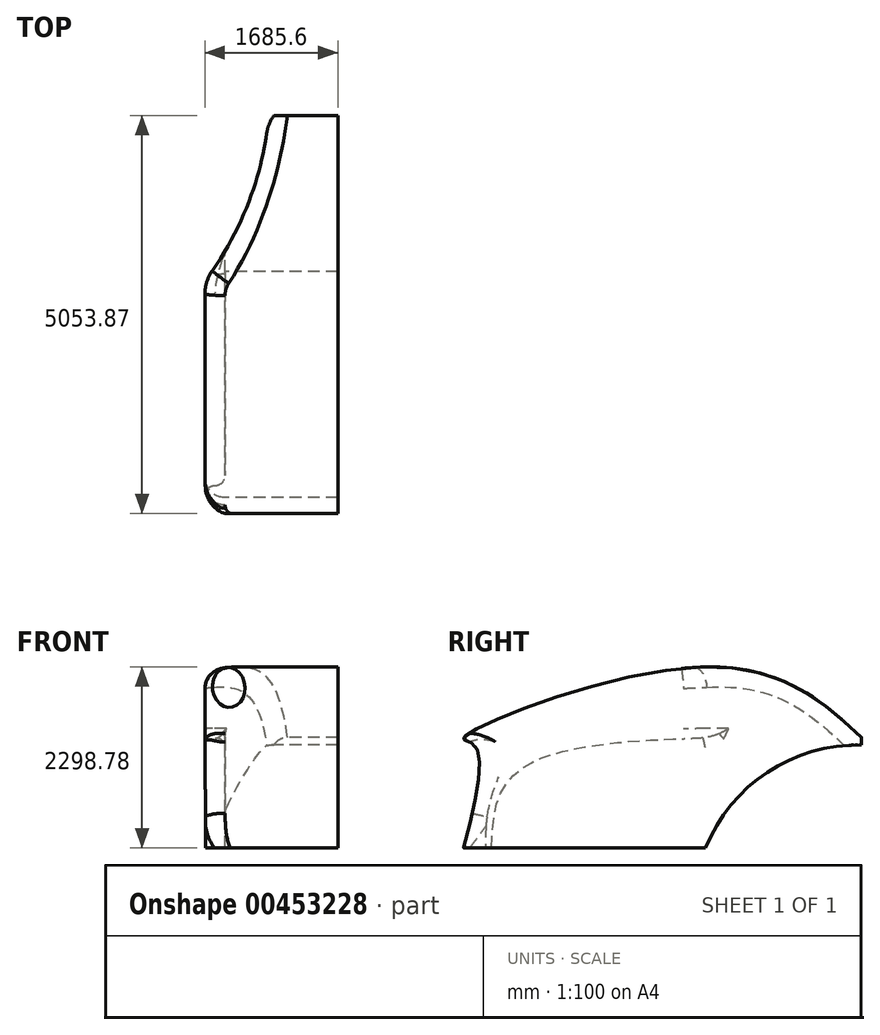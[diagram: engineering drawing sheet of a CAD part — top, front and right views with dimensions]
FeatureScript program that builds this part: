
annotation { "Feature Type Name" : "Feature", "Feature Type Description" : "" }
export const myFeature = defineFeature(function(context is Context, id is Id, definition is map)
    precondition{}
    {
        {
            var Q0;
            Q0=qCreatedBy(makeId("Top.planeOp"),FACE);
            var sketch = newSketch(context, id + "F0", { "sketchPlane" : qUnion([Q0])});
            skLineSegment(sketch, "E0.bottom", {"start": v(-854.4, 72.9) * mm, "end": v(-2159, 72.9) * mm});
            skLineSegment(sketch, "E0.top", {"start": v(-854.4, 5152.9) * mm, "end": v(-1731.8, 5152.9) * mm});
            skLineSegment(sketch, "E0.right", {"start": v(-2540, 453.9) * mm, "end": v(-2540, 2892.85) * mm});
            skPoint(sketch, "E1.visualSharp", {"position": v(-2540, 72.9) * mm});
            skArc(sketch, "E1.filletArc", {"start": v(-2540, 453.9) * mm, "mid": v(-2428.4, 184.5) * mm, "end": v(-2159, 72.9) * mm});
            skArc(sketch, "E2", {"start": v(-2447.98, 3184.45) * mm, "mid": v(-1959.99, 4121.41) * mm, "end": v(-1731.8, 5152.9) * mm});
            skLineSegment(sketch, "E3", {"start": v(-854.4, 5152.9) * mm, "end": v(-854.4, 72.9) * mm});
            skPoint(sketch, "E0.left.end.orphan", {"position": v(23, 5152.9) * mm});
            skPoint(sketch, "E4.visualSharp", {"position": v(-2540, 3058.43) * mm});
            skArc(sketch, "E4.filletArc", {"start": v(-2447.98, 3184.45) * mm, "mid": v(-2516.45, 3045.74) * mm, "end": v(-2540, 2892.85) * mm});
            skSolve(sketch);
        }
        {
            var Q0;
            Q0=makeQuery(id+"F0.imprint","IMPRINT",FACE,{"disambiguationData":[TD([[makeQuery(id+"F0.imprint","IMPRINT",EDGE,{"derivedFrom":sQuery(id+"F0.wireOp",EDGE,"E0.bottom")}),-1.0]])]});
            extrude(context, id + "F1", {"entities" : qUnion([Q0]), "depth" : 2540 * mm});
        }
        {
            var Q0;
            Q0=makeQuery(id+"F1.opExtrude","SWEPT_FACE",FACE,{"disambiguationData":[OSD([sQuery(id+"F0.wireOp",EDGE,"E0.right")])]});
            var sketch = newSketch(context, id + "F2", { "sketchPlane" : qUnion([Q0])});
            skArc(sketch, "E5", {"start": v(-3170.36, 0) * mm, "mid": v(-4005.04, 991.77) * mm, "end": v(-5263.88, 1301.03) * mm});
            skPoint(sketch, "E6.3.internal.snap0", {"position": v(-4005.04, 991.77) * mm});
            skPoint(sketch, "E6.3.internal.orphan", {"position": v(-99.2, 991.77) * mm});
            skFitSpline(sketch, "E7", {"points": [v(-5263.88, 1301.03) * mm, v(-3180.23, 2298.41) * mm, v(-99.2, 1389.9) * mm, v(-237.45, 1301.03) * mm, v(-99.2, 0) * mm], "startDerivative": vector(5128.45, 4861.95) * mm, "endDerivative": vector(1834.22, -7313.57) * mm});
            skLineSegment(sketch, "E8.bottom", {"start": v(-5431.75, -160.49) * mm, "end": v(750.06, -160.49) * mm});
            skLineSegment(sketch, "E8.top", {"start": v(-5431.75, 3009.42) * mm, "end": v(750.06, 3009.42) * mm});
            skLineSegment(sketch, "E8.left", {"start": v(-5431.75, -160.49) * mm, "end": v(-5431.75, 3009.42) * mm});
            skLineSegment(sketch, "E8.right", {"start": v(750.06, -160.49) * mm, "end": v(750.06, 3009.42) * mm});
            skLineSegment(sketch, "E9", {"start": v(-3170.36, 0) * mm, "end": v(-99.2, 0) * mm});
            skSolve(sketch);
        }
        {
            var Q0;
            {var subQ1=sQuery(id+"F0.wireOp",EDGE,"E0.right");var subQ6=makeQuery(id+"F1.opExtrude","CAP_EDGE",EDGE,{"disambiguationData":[OSD([subQ1])],"isStart":false});Q0=makeQuery(id+"F2.imprint","IMPRINT",FACE,{"disambiguationData":[TD([[makeQuery(id+"F2.imprint","IMPRINT",EDGE,{"derivedFrom":subQ6}),1.0]])]});}
            var Q1;
            {var subQ8=sQuery(id+"F2.wireOp",EDGE,"E5");Q1=makeQuery(id+"F2.imprint","IMPRINT",FACE,{"disambiguationData":[TD([[makeQuery(id+"F2.imprint","IMPRINT",EDGE,{"derivedFrom":subQ8}),1.0]])]});}
            extrude(context, id + "F3", {"entities" : qUnion([Q0, Q1]), "operationType" : NewBodyOperationType.REMOVE, "endBound" : BoundingType.THROUGH_ALL, "oppositeDirection" : true, "depth" : 25.4 * mm});
        }
        {
            var Q0;
            Q0=makeQuery(id+"F3.boolean.opBoolean","INTERSECT",EDGE,{"derivedFrom":[makeQuery(id+"F1.opExtrude","SWEPT_FACE",FACE,{"disambiguationData":[OSD([sQuery(id+"F0.wireOp",EDGE,"E2")])]}),makeQuery(id+"F3.opExtrude","SWEPT_FACE",FACE,{"disambiguationData":[OSD([sQuery(id+"F2.wireOp",EDGE,"E7")])]})]});
            var Q1;
            Q1=makeQuery(id+"F3.boolean.opBoolean","INTERSECT",EDGE,{"derivedFrom":[makeQuery(id+"F1.opExtrude","SWEPT_FACE",FACE,{"disambiguationData":[OSD([sQuery(id+"F0.wireOp",EDGE,"E4.filletArc")])]}),makeQuery(id+"F3.opExtrude","SWEPT_FACE",FACE,{"disambiguationData":[OSD([sQuery(id+"F2.wireOp",EDGE,"E7")])]})]});
            var Q2;
            Q2=makeQuery(id+"F3.boolean.opBoolean","COPY",EDGE,{"derivedFrom":makeQuery(id+"F3.opExtrude","CAP_EDGE",EDGE,{"disambiguationData":[OSD([sQuery(id+"F2.wireOp",EDGE,"E7")])],"isStart":true})});
            var Q3;
            Q3=makeQuery(id+"F3.boolean.opBoolean","INTERSECT",EDGE,{"derivedFrom":[makeQuery(id+"F1.opExtrude","SWEPT_FACE",FACE,{"disambiguationData":[OSD([sQuery(id+"F0.wireOp",EDGE,"E1.filletArc")])]}),makeQuery(id+"F3.opExtrude","SWEPT_FACE",FACE,{"disambiguationData":[OSD([sQuery(id+"F2.wireOp",EDGE,"E7")])]})]});
            fillet(context, id + "F4", {"entities" : qUnion([Q0, Q1, Q2, Q3]), "radius" : 254 * mm, "tangentPropagation" : true, "allowEdgeOverflow" : false});
        }
        {
            var Q0;
            Q0=makeQuery(id+"F1.opExtrude","SWEPT_FACE",FACE,{"disambiguationData":[OSD([sQuery(id+"F0.wireOp",EDGE,"E0.right")])]});
            var sketch = newSketch(context, id + "F5", { "sketchPlane" : qUnion([Q0])});
            skFitSpline(sketch, "E10", {"points": [v(-453.9, 0) * mm, v(-1083.3, 1139.36) * mm, v(-5151.78, 1318.3) * mm, v(-5156.49, 1318.3) * mm], "startDerivative": vector(-122, 3820.9) * mm, "endDerivative": vector(-69.89, 12.68) * mm});
            skLineSegment(sketch, "E11", {"start": v(-5151.78, 1318.3) * mm, "end": v(-3150.5, -122.62) * mm});
            skLineSegment(sketch, "E12", {"start": v(-3150.5, -122.62) * mm, "end": v(-453.9, 0) * mm});
            skSolve(sketch);
        }
        {
            var Q0;
            {var subQ1=sQuery(id+"F0.wireOp",EDGE,"E0.right");var subQ2=makeQuery(id+"F1.opExtrude","CAP_EDGE",EDGE,{"disambiguationData":[OSD([subQ1])],"isStart":true});Q0=makeQuery(id+"F5.imprint","IMPRINT",FACE,{"disambiguationData":[TD([[makeQuery(id+"F5.imprint","IMPRINT",EDGE,{"derivedFrom":subQ2}),-1.0]])]});}
            var Q1;
            {var subQ2=sQuery(id+"F5.wireOp",EDGE,"E11");Q1=makeQuery(id+"F5.imprint","IMPRINT",FACE,{"disambiguationData":[TD([[makeQuery(id+"F5.imprint","IMPRINT",EDGE,{"derivedFrom":subQ2}),1.0]])]});}
            extrude(context, id + "F6", {"entities" : qUnion([Q0, Q1]), "operationType" : NewBodyOperationType.REMOVE, "oppositeDirection" : true, "depth" : 254 * mm});
        }
        {
            var Q0;
            Q0=makeQuery(id+"F6.boolean.opBoolean","COPY",EDGE,{"derivedFrom":makeQuery(id+"F6.opExtrude","CAP_EDGE",EDGE,{"disambiguationData":[OSD([sQuery(id+"F5.wireOp",EDGE,"E10")])],"isStart":true})});
            var Q1;
            Q1=makeQuery(id+"F6.boolean.opBoolean","INTERSECT",EDGE,{"derivedFrom":[makeQuery(id+"F1.opExtrude","SWEPT_FACE",FACE,{"disambiguationData":[OSD([sQuery(id+"F0.wireOp",EDGE,"E2")])]}),makeQuery(id+"F6.opExtrude","CAP_FACE",FACE,{"disambiguationData":[OSD([sQuery(id+"F5.wireOp",EDGE,"E10"),sQuery(id+"F5.wireOp",EDGE,"E11"),sQuery(id+"F5.wireOp",EDGE,"E12")])],"isStart":false})]});
            var Q2;
            Q2=makeQuery(id+"F6.boolean.opBoolean","INTERSECT",EDGE,{"derivedFrom":[makeQuery(id+"F1.opExtrude","SWEPT_FACE",FACE,{"disambiguationData":[OSD([sQuery(id+"F0.wireOp",EDGE,"E2")])]}),makeQuery(id+"F6.opExtrude","SWEPT_FACE",FACE,{"disambiguationData":[OSD([sQuery(id+"F5.wireOp",EDGE,"E10")])]})]});
            var Q3;
            Q3=makeQuery(id+"F6.boolean.opBoolean","INTERSECT",EDGE,{"derivedFrom":[makeQuery(id+"F1.opExtrude","SWEPT_FACE",FACE,{"disambiguationData":[OSD([sQuery(id+"F0.wireOp",EDGE,"E4.filletArc")])]}),makeQuery(id+"F6.opExtrude","SWEPT_FACE",FACE,{"disambiguationData":[OSD([sQuery(id+"F5.wireOp",EDGE,"E10")])]})]});
            fillet(context, id + "F7", {"entities" : qUnion([Q0, Q1, Q2, Q3]), "radius" : 127 * mm, "tangentPropagation" : true, "allowEdgeOverflow" : false});
        }
        {
            var Q0;
            {var subQ0=sQuery(id+"F5.wireOp",EDGE,"E10");Q0=makeQuery(id+"F7.opFillet","BLEND_EDGE",EDGE,{"blendedFrom":[makeQuery(id+"F6.boolean.opBoolean","INTERSECT",EDGE,{"derivedFrom":[makeQuery(id+"F1.opExtrude","SWEPT_FACE",FACE,{"disambiguationData":[OSD([sQuery(id+"F0.wireOp",EDGE,"E2")])]}),makeQuery(id+"F6.opExtrude","SWEPT_FACE",FACE,{"disambiguationData":[OSD([subQ0])]})]}),makeQuery(id+"F6.boolean.opBoolean","COPY",FACE,{"derivedFrom":makeQuery(id+"F6.opExtrude","CAP_FACE",FACE,{"disambiguationData":[OSD([subQ0,sQuery(id+"F5.wireOp",EDGE,"E11"),sQuery(id+"F5.wireOp",EDGE,"E12")])],"isStart":false})})],"blendedInto":[makeQuery(id+"F6.boolean.opBoolean","COPY",FACE,{"derivedFrom":makeQuery(id+"F6.opExtrude","CAP_FACE",FACE,{"disambiguationData":[OSD([subQ0,sQuery(id+"F5.wireOp",EDGE,"E11"),sQuery(id+"F5.wireOp",EDGE,"E12")])],"isStart":false})})]});}
            var Q1;
            Q1=makeQuery(id+"F6.boolean.opBoolean","COPY",EDGE,{"derivedFrom":makeQuery(id+"F6.opExtrude","CAP_EDGE",EDGE,{"disambiguationData":[OSD([sQuery(id+"F5.wireOp",EDGE,"E10")])],"isStart":false})});
            fillet(context, id + "F8", {"entities" : qUnion([Q0, Q1]), "radius" : 127 * mm, "tangentPropagation" : true, "allowEdgeOverflow" : false});
        }
    });
